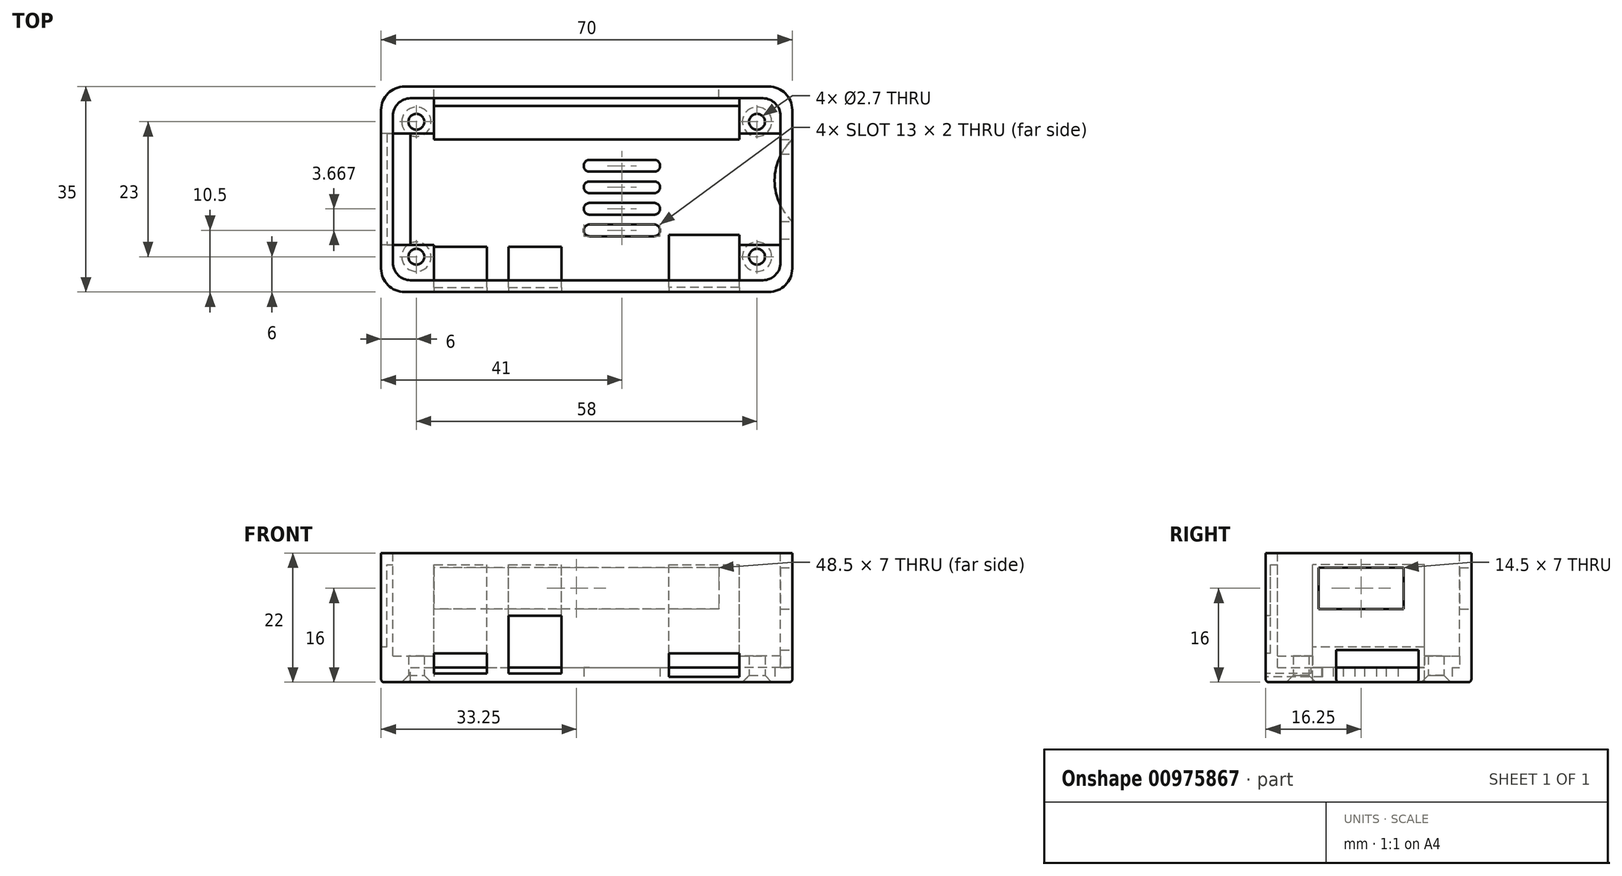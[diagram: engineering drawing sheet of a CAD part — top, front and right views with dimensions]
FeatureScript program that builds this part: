
annotation { "Feature Type Name" : "Feature", "Feature Type Description" : "" }
export const myFeature = defineFeature(function(context is Context, id is Id, definition is map)
    precondition{}
    {
        {
            var Q0;
            Q0=qCreatedBy(makeId("Top.planeOp"),FACE);
            var sketch = newSketch(context, id + "F0", { "sketchPlane" : qUnion([Q0])});
            skLineSegment(sketch, "E0.bottom", {"start": v(-31, 17.5) * mm, "end": v(31, 17.5) * mm});
            skLineSegment(sketch, "E0.top", {"start": v(-31, -17.5) * mm, "end": v(31, -17.5) * mm});
            skLineSegment(sketch, "E0.left", {"start": v(-35, 13.5) * mm, "end": v(-35, -13.5) * mm});
            skLineSegment(sketch, "E0.right", {"start": v(35, 13.5) * mm, "end": v(35, -13.5) * mm});
            skPoint(sketch, "E1.visualSharp", {"position": v(-35, 17.5) * mm});
            skArc(sketch, "E1.filletArc", {"start": v(-31, 17.5) * mm, "mid": v(-33.83, 16.33) * mm, "end": v(-35, 13.5) * mm});
            skPoint(sketch, "E2.visualSharp", {"position": v(35, 17.5) * mm});
            skArc(sketch, "E2.filletArc", {"start": v(35, 13.5) * mm, "mid": v(33.83, 16.33) * mm, "end": v(31, 17.5) * mm});
            skPoint(sketch, "E3.visualSharp", {"position": v(-35, -17.5) * mm});
            skArc(sketch, "E3.filletArc", {"start": v(-35, -13.5) * mm, "mid": v(-33.83, -16.33) * mm, "end": v(-31, -17.5) * mm});
            skPoint(sketch, "E4.visualSharp", {"position": v(35, -17.5) * mm});
            skArc(sketch, "E4.filletArc", {"start": v(31, -17.5) * mm, "mid": v(33.83, -16.33) * mm, "end": v(35, -13.5) * mm});
            skSolve(sketch);
        }
        {
            var Q0;
            Q0=makeQuery(id+"F0.imprint","IMPRINT",FACE,{"disambiguationData":[TD([[makeQuery(id+"F0.imprint","IMPRINT",EDGE,{"derivedFrom":sQuery(id+"F0.wireOp",EDGE,"E0.bottom")}),-1.0]])]});
            extrude(context, id + "F1", {"entities" : qUnion([Q0]), "depth" : 22 * mm, "offsetDistance" : 25 * mm});
        }
        {
            var Q0;
            Q0=makeQuery(id+"F1.opExtrude","CAP_FACE",FACE,{"disambiguationData":[OSD([sQuery(id+"F0.wireOp",EDGE,"E0.bottom"),sQuery(id+"F0.wireOp",EDGE,"E0.top"),sQuery(id+"F0.wireOp",EDGE,"E0.left"),sQuery(id+"F0.wireOp",EDGE,"E0.right"),sQuery(id+"F0.wireOp",EDGE,"E1.filletArc"),sQuery(id+"F0.wireOp",EDGE,"E2.filletArc"),sQuery(id+"F0.wireOp",EDGE,"E3.filletArc"),sQuery(id+"F0.wireOp",EDGE,"E4.filletArc")])],"isStart":false});
            var sketch = newSketch(context, id + "F2", { "sketchPlane" : qUnion([Q0])});
            skLineSegment(sketch, "E5.bottom", {"start": v(-30, 15.5) * mm, "end": v(30, 15.5) * mm});
            skLineSegment(sketch, "E5.top", {"start": v(-30, -15.5) * mm, "end": v(30, -15.5) * mm});
            skLineSegment(sketch, "E5.left", {"start": v(-33, 12.5) * mm, "end": v(-33, -12.5) * mm});
            skLineSegment(sketch, "E5.right", {"start": v(33, 12.5) * mm, "end": v(33, -12.5) * mm});
            skPoint(sketch, "E6.visualSharp", {"position": v(-33, 15.5) * mm});
            skArc(sketch, "E6.filletArc", {"start": v(-30, 15.5) * mm, "mid": v(-32.12, 14.62) * mm, "end": v(-33, 12.5) * mm});
            skPoint(sketch, "E7.visualSharp", {"position": v(-33, -15.5) * mm});
            skArc(sketch, "E7.filletArc", {"start": v(-33, -12.5) * mm, "mid": v(-32.12, -14.62) * mm, "end": v(-30, -15.5) * mm});
            skPoint(sketch, "E8.visualSharp", {"position": v(33, 15.5) * mm});
            skArc(sketch, "E8.filletArc", {"start": v(33, 12.5) * mm, "mid": v(32.12, 14.62) * mm, "end": v(30, 15.5) * mm});
            skPoint(sketch, "E9.visualSharp", {"position": v(33, -15.5) * mm});
            skArc(sketch, "E9.filletArc", {"start": v(30, -15.5) * mm, "mid": v(32.12, -14.62) * mm, "end": v(33, -12.5) * mm});
            skSolve(sketch);
        }
        {
            var Q0;
            Q0=makeQuery(id+"F2.imprint","IMPRINT",FACE,{"disambiguationData":[TD([[makeQuery(id+"F2.imprint","IMPRINT",EDGE,{"derivedFrom":sQuery(id+"F2.wireOp",EDGE,"E5.bottom")}),-1.0]])]});
            extrude(context, id + "F3", {"entities" : qUnion([Q0]), "operationType" : NewBodyOperationType.REMOVE, "oppositeDirection" : true, "depth" : 19.5 * mm, "offsetDistance" : 25 * mm});
        }
        {
            var Q0;
            Q0=makeQuery(id+"F1.opExtrude","SWEPT_FACE",FACE,{"disambiguationData":[OSD([sQuery(id+"F0.wireOp",EDGE,"E0.top")])]});
            var sketch = newSketch(context, id + "F4", { "sketchPlane" : qUnion([Q0])});
            skLineSegment(sketch, "E10.bottom", {"start": v(-26, 1.5) * mm, "end": v(-17, 1.5) * mm});
            skLineSegment(sketch, "E10.top", {"start": v(-26, 4.9) * mm, "end": v(-17, 4.9) * mm});
            skLineSegment(sketch, "E10.left", {"start": v(-26, 1.5) * mm, "end": v(-26, 4.9) * mm});
            skLineSegment(sketch, "E10.right", {"start": v(-17, 1.5) * mm, "end": v(-17, 4.9) * mm});
            skLineSegment(sketch, "E11.bottom", {"start": v(-13.3, 1.5) * mm, "end": v(-4.3, 1.5) * mm});
            skLineSegment(sketch, "E11.top", {"start": v(-13.3, 11.3) * mm, "end": v(-4.3, 11.3) * mm});
            skLineSegment(sketch, "E11.left", {"start": v(-13.3, 1.5) * mm, "end": v(-13.3, 11.3) * mm});
            skLineSegment(sketch, "E11.right", {"start": v(-4.3, 1.5) * mm, "end": v(-4.3, 11.3) * mm});
            skLineSegment(sketch, "E12.bottom", {"start": v(26, 0.9) * mm, "end": v(14, 0.9) * mm});
            skLineSegment(sketch, "E12.top", {"start": v(26, 4.9) * mm, "end": v(14, 4.9) * mm});
            skLineSegment(sketch, "E12.left", {"start": v(26, 0.9) * mm, "end": v(26, 4.9) * mm});
            skLineSegment(sketch, "E12.right", {"start": v(14, 0.9) * mm, "end": v(14, 4.9) * mm});
            skSolve(sketch);
        }
        {
            var Q0;
            Q0=makeQuery(id+"F4.imprint","IMPRINT",FACE,{"disambiguationData":[TD([[makeQuery(id+"F4.imprint","IMPRINT",EDGE,{"derivedFrom":sQuery(id+"F4.wireOp",EDGE,"E10.bottom")}),1.0]])]});
            extrude(context, id + "F5", {"entities" : qUnion([Q0]), "operationType" : NewBodyOperationType.REMOVE, "oppositeDirection" : true, "depth" : 7.7 * mm, "offsetDistance" : 25 * mm});
        }
        {
            var Q0;
            Q0=makeQuery(id+"F4.imprint","IMPRINT",FACE,{"disambiguationData":[TD([[makeQuery(id+"F4.imprint","IMPRINT",EDGE,{"derivedFrom":sQuery(id+"F4.wireOp",EDGE,"E11.bottom")}),1.0]])]});
            extrude(context, id + "F6", {"entities" : qUnion([Q0]), "operationType" : NewBodyOperationType.REMOVE, "oppositeDirection" : true, "depth" : 7.7 * mm, "offsetDistance" : 25 * mm});
        }
        {
            var Q0;
            Q0=makeQuery(id+"F4.imprint","IMPRINT",FACE,{"disambiguationData":[TD([[makeQuery(id+"F4.imprint","IMPRINT",EDGE,{"derivedFrom":sQuery(id+"F4.wireOp",EDGE,"E12.bottom")}),-1.0]])]});
            extrude(context, id + "F7", {"entities" : qUnion([Q0]), "operationType" : NewBodyOperationType.REMOVE, "oppositeDirection" : true, "depth" : 9.7 * mm, "offsetDistance" : 25 * mm});
        }
        {
            var Q0;
            Q0=makeQuery(id+"F3.boolean.opBoolean","COPY",FACE,{"derivedFrom":makeQuery(id+"F3.opExtrude","CAP_FACE",FACE,{"disambiguationData":[OSD([sQuery(id+"F2.wireOp",EDGE,"E5.bottom"),sQuery(id+"F2.wireOp",EDGE,"E5.top"),sQuery(id+"F2.wireOp",EDGE,"E5.left"),sQuery(id+"F2.wireOp",EDGE,"E5.right"),sQuery(id+"F2.wireOp",EDGE,"E6.filletArc"),sQuery(id+"F2.wireOp",EDGE,"E7.filletArc"),sQuery(id+"F2.wireOp",EDGE,"E8.filletArc"),sQuery(id+"F2.wireOp",EDGE,"E9.filletArc")])],"isStart":false})});
            var sketch = newSketch(context, id + "F8", { "sketchPlane" : qUnion([Q0])});
            skLineSegment(sketch, "E13.bottom", {"start": v(-33, 9.5) * mm, "end": v(-26, 9.5) * mm});
            skLineSegment(sketch, "E13.top", {"start": v(-33, 15.5) * mm, "end": v(-26, 15.5) * mm});
            skLineSegment(sketch, "E13.left", {"start": v(-33, 9.5) * mm, "end": v(-33, 15.5) * mm});
            skLineSegment(sketch, "E13.right", {"start": v(-26, 9.5) * mm, "end": v(-26, 15.5) * mm});
            skLineSegment(sketch, "E14.bottom", {"start": v(-33, -9.5) * mm, "end": v(-26, -9.5) * mm});
            skLineSegment(sketch, "E14.top", {"start": v(-33, -15.5) * mm, "end": v(-26, -15.5) * mm});
            skLineSegment(sketch, "E14.left", {"start": v(-33, -9.5) * mm, "end": v(-33, -15.5) * mm});
            skLineSegment(sketch, "E14.right", {"start": v(-26, -9.5) * mm, "end": v(-26, -15.5) * mm});
            skLineSegment(sketch, "E15.bottom", {"start": v(33, -9.5) * mm, "end": v(26, -9.5) * mm});
            skLineSegment(sketch, "E15.top", {"start": v(33, -15.5) * mm, "end": v(26, -15.5) * mm});
            skLineSegment(sketch, "E15.left", {"start": v(33, -9.5) * mm, "end": v(33, -15.5) * mm});
            skLineSegment(sketch, "E15.right", {"start": v(26, -9.5) * mm, "end": v(26, -15.5) * mm});
            skLineSegment(sketch, "E16.bottom", {"start": v(33, 9.5) * mm, "end": v(26, 9.5) * mm});
            skLineSegment(sketch, "E16.top", {"start": v(33, 15.5) * mm, "end": v(26, 15.5) * mm});
            skLineSegment(sketch, "E16.left", {"start": v(33, 9.5) * mm, "end": v(33, 15.5) * mm});
            skLineSegment(sketch, "E16.right", {"start": v(26, 9.5) * mm, "end": v(26, 15.5) * mm});
            skSolve(sketch);
        }
        {
            var Q0;
            {var subQ2=sQuery(id+"F8.wireOp",EDGE,"E13.bottom");Q0=makeQuery(id+"F8.imprint","IMPRINT",FACE,{"disambiguationData":[TD([[makeQuery(id+"F8.imprint","IMPRINT",EDGE,{"derivedFrom":subQ2}),1.0]])]});}
            var Q1;
            {var subQ3=sQuery(id+"F8.wireOp",EDGE,"E14.bottom");Q1=makeQuery(id+"F8.imprint","IMPRINT",FACE,{"disambiguationData":[TD([[makeQuery(id+"F8.imprint","IMPRINT",EDGE,{"derivedFrom":subQ3}),-1.0]])]});}
            var Q2;
            {var subQ2=sQuery(id+"F8.wireOp",EDGE,"E16.bottom");Q2=makeQuery(id+"F8.imprint","IMPRINT",FACE,{"disambiguationData":[TD([[makeQuery(id+"F8.imprint","IMPRINT",EDGE,{"derivedFrom":subQ2}),-1.0]])]});}
            var Q3;
            {var subQ2=sQuery(id+"F8.wireOp",EDGE,"E15.bottom");Q3=makeQuery(id+"F8.imprint","IMPRINT",FACE,{"disambiguationData":[TD([[makeQuery(id+"F8.imprint","IMPRINT",EDGE,{"derivedFrom":subQ2}),1.0]])]});}
            extrude(context, id + "F9", {"entities" : qUnion([Q0, Q1, Q2, Q3]), "operationType" : NewBodyOperationType.ADD, "depth" : 2 * mm, "offsetDistance" : 25 * mm});
        }
        {
            var Q0;
            Q0=makeQuery(id+"F1.opExtrude","SWEPT_FACE",FACE,{"disambiguationData":[OSD([sQuery(id+"F0.wireOp",EDGE,"E0.right")])]});
            var sketch = newSketch(context, id + "F10", { "sketchPlane" : qUnion([Q0])});
            skLineSegment(sketch, "E17.bottom", {"start": v(8.5, 2.5) * mm, "end": v(-5.5, 2.5) * mm});
            skLineSegment(sketch, "E17.top", {"start": v(8.5, 5.5) * mm, "end": v(-5.5, 5.5) * mm});
            skLineSegment(sketch, "E17.left", {"start": v(8.5, 2.5) * mm, "end": v(8.5, 5.5) * mm});
            skLineSegment(sketch, "E17.right", {"start": v(-5.5, 2.5) * mm, "end": v(-5.5, 5.5) * mm});
            skSolve(sketch);
        }
        {
            var Q0;
            Q0=makeQuery(id+"F10.imprint","IMPRINT",FACE,{"disambiguationData":[TD([[makeQuery(id+"F10.imprint","IMPRINT",EDGE,{"derivedFrom":sQuery(id+"F10.wireOp",EDGE,"E17.bottom")}),-1.0]])]});
            var Q1;
            Q1=makeQuery(id+"F3.boolean.opBoolean","COPY",FACE,{"derivedFrom":makeQuery(id+"F3.opExtrude","SWEPT_FACE",FACE,{"disambiguationData":[OSD([sQuery(id+"F2.wireOp",EDGE,"E5.right")])]})});
            extrude(context, id + "F11", {"entities" : qUnion([Q0]), "operationType" : NewBodyOperationType.REMOVE, "endBound" : BoundingType.UP_TO_SURFACE, "oppositeDirection" : true, "depth" : 25 * mm, "endBoundEntityFace" : qUnion([Q1]), "offsetDistance" : 25 * mm});
        }
        {
            var Q0;
            Q0=makeQuery(id+"F1.opExtrude","CAP_FACE",FACE,{"disambiguationData":[OSD([sQuery(id+"F0.wireOp",EDGE,"E0.bottom"),sQuery(id+"F0.wireOp",EDGE,"E0.top"),sQuery(id+"F0.wireOp",EDGE,"E0.left"),sQuery(id+"F0.wireOp",EDGE,"E0.right"),sQuery(id+"F0.wireOp",EDGE,"E1.filletArc"),sQuery(id+"F0.wireOp",EDGE,"E2.filletArc"),sQuery(id+"F0.wireOp",EDGE,"E3.filletArc"),sQuery(id+"F0.wireOp",EDGE,"E4.filletArc")])],"isStart":true});
            var sketch = newSketch(context, id + "F12", { "sketchPlane" : qUnion([Q0])});
            skPoint(sketch, "E18", {"position": v(35, 5.5) * mm});
            skPoint(sketch, "E19", {"position": v(35, -8.5) * mm});
            skPoint(sketch, "E20", {"position": v(32, -1.5) * mm});
            skArc(sketch, "E21", {"start": v(35, 5.5) * mm, "mid": v(32, -1.5) * mm, "end": v(35, -8.5) * mm});
            skLineSegment(sketch, "E22", {"start": v(35, 5.5) * mm, "end": v(35, -8.5) * mm});
            skSolve(sketch);
        }
        {
            var Q0;
            Q0=makeQuery(id+"F12.imprint","IMPRINT",FACE,{"disambiguationData":[TD([[makeQuery(id+"F12.imprint","IMPRINT",EDGE,{"derivedFrom":sQuery(id+"F12.wireOp",EDGE,"E21")}),1.0]])]});
            extrude(context, id + "F13", {"entities" : qUnion([Q0]), "operationType" : NewBodyOperationType.REMOVE, "oppositeDirection" : true, "depth" : 3 * mm, "offsetDistance" : 25 * mm});
        }
        {
            var Q0;
            Q0=makeQuery(id+"F1.opExtrude","SWEPT_FACE",FACE,{"disambiguationData":[OSD([sQuery(id+"F0.wireOp",EDGE,"E0.left")])]});
            var sketch = newSketch(context, id + "F14", { "sketchPlane" : qUnion([Q0])});
            skLineSegment(sketch, "E23.bottom", {"start": v(-9.5, 0) * mm, "end": v(9.5, 0) * mm});
            skLineSegment(sketch, "E23.top", {"start": v(-9.5, 6) * mm, "end": v(9.5, 6) * mm});
            skLineSegment(sketch, "E23.left", {"start": v(-9.5, 0) * mm, "end": v(-9.5, 6) * mm});
            skLineSegment(sketch, "E23.right", {"start": v(9.5, 0) * mm, "end": v(9.5, 6) * mm});
            skSolve(sketch);
        }
        {
            var Q0;
            Q0=makeQuery(id+"F14.imprint","IMPRINT",FACE,{"disambiguationData":[TD([[makeQuery(id+"F14.imprint","IMPRINT",EDGE,{"derivedFrom":sQuery(id+"F14.wireOp",EDGE,"E23.bottom")}),1.0]])]});
            var Q1;
            Q1=makeQuery(id+"F3.boolean.opBoolean","COPY",FACE,{"derivedFrom":makeQuery(id+"F3.opExtrude","SWEPT_FACE",FACE,{"disambiguationData":[OSD([sQuery(id+"F2.wireOp",EDGE,"E5.left")])]})});
            extrude(context, id + "F15", {"entities" : qUnion([Q0]), "operationType" : NewBodyOperationType.REMOVE, "oppositeDirection" : true, "depth" : 5 * mm, "endBoundEntityFace" : qUnion([Q1]), "offsetDistance" : 25 * mm});
        }
        {
            var Q0;
            Q0=makeQuery(id+"F1.opExtrude","SWEPT_FACE",FACE,{"disambiguationData":[OSD([sQuery(id+"F0.wireOp",EDGE,"E0.bottom")])]});
            var sketch = newSketch(context, id + "F16", { "sketchPlane" : qUnion([Q0])});
            skLineSegment(sketch, "E24.bottom", {"start": v(-22.5, 19.5) * mm, "end": v(26, 19.5) * mm});
            skLineSegment(sketch, "E24.top", {"start": v(-22.5, 12.5) * mm, "end": v(26, 12.5) * mm});
            skLineSegment(sketch, "E24.left", {"start": v(-22.5, 19.5) * mm, "end": v(-22.5, 12.5) * mm});
            skLineSegment(sketch, "E24.right", {"start": v(26, 19.5) * mm, "end": v(26, 12.5) * mm});
            skSolve(sketch);
        }
        {
            var Q0;
            Q0=makeQuery(id+"F16.imprint","IMPRINT",FACE,{"disambiguationData":[TD([[makeQuery(id+"F16.imprint","IMPRINT",EDGE,{"derivedFrom":sQuery(id+"F16.wireOp",EDGE,"E24.bottom")}),-1.0]])]});
            extrude(context, id + "F17", {"entities" : qUnion([Q0]), "operationType" : NewBodyOperationType.REMOVE, "endBound" : BoundingType.UP_TO_NEXT, "oppositeDirection" : true, "depth" : 25 * mm, "offsetDistance" : 25 * mm});
        }
        {
            var Q0;
            Q0=makeQuery(id+"F1.opExtrude","SWEPT_FACE",FACE,{"disambiguationData":[OSD([sQuery(id+"F0.wireOp",EDGE,"E0.right")])]});
            var sketch = newSketch(context, id + "F18", { "sketchPlane" : qUnion([Q0])});
            skLineSegment(sketch, "E25.bottom", {"start": v(-8.5, 19.5) * mm, "end": v(6, 19.5) * mm});
            skLineSegment(sketch, "E25.top", {"start": v(-8.5, 12.5) * mm, "end": v(6, 12.5) * mm});
            skLineSegment(sketch, "E25.left", {"start": v(-8.5, 19.5) * mm, "end": v(-8.5, 12.5) * mm});
            skLineSegment(sketch, "E25.right", {"start": v(6, 19.5) * mm, "end": v(6, 12.5) * mm});
            skSolve(sketch);
        }
        {
            var Q0;
            Q0=makeQuery(id+"F18.imprint","IMPRINT",FACE,{"disambiguationData":[TD([[makeQuery(id+"F18.imprint","IMPRINT",EDGE,{"derivedFrom":sQuery(id+"F18.wireOp",EDGE,"E25.bottom")}),-1.0]])]});
            extrude(context, id + "F19", {"entities" : qUnion([Q0]), "operationType" : NewBodyOperationType.REMOVE, "endBound" : BoundingType.UP_TO_NEXT, "oppositeDirection" : true, "depth" : 25 * mm, "offsetDistance" : 25 * mm});
        }
        {
            var Q0;
            Q0=makeQuery(id+"F1.opExtrude","CAP_FACE",FACE,{"disambiguationData":[OSD([sQuery(id+"F0.wireOp",EDGE,"E0.bottom"),sQuery(id+"F0.wireOp",EDGE,"E0.top"),sQuery(id+"F0.wireOp",EDGE,"E0.left"),sQuery(id+"F0.wireOp",EDGE,"E0.right"),sQuery(id+"F0.wireOp",EDGE,"E1.filletArc"),sQuery(id+"F0.wireOp",EDGE,"E2.filletArc"),sQuery(id+"F0.wireOp",EDGE,"E3.filletArc"),sQuery(id+"F0.wireOp",EDGE,"E4.filletArc")])],"isStart":true});
            var sketch = newSketch(context, id + "F20", { "sketchPlane" : qUnion([Q0])});
            skPoint(sketch, "E26", {"position": v(-29, 11.5) * mm});
            skPoint(sketch, "E27", {"position": v(-29, -11.5) * mm});
            skPoint(sketch, "E28", {"position": v(29, -11.5) * mm});
            skPoint(sketch, "E29", {"position": v(29, 11.5) * mm});
            skSolve(sketch);
        }
        {
            var Q0;
            Q0=sQuery(id+"F20.wireOp",VERTEX,"E26");
            var Q1;
            Q1=makeQuery(id+"F1.opExtrude","SWEPT_BODY",BODY,{"disambiguationData":[OSD([sQuery(id+"F0.wireOp",EDGE,"E0.bottom"),sQuery(id+"F0.wireOp",EDGE,"E0.top"),sQuery(id+"F0.wireOp",EDGE,"E0.left"),sQuery(id+"F0.wireOp",EDGE,"E0.right"),sQuery(id+"F0.wireOp",EDGE,"E1.filletArc"),sQuery(id+"F0.wireOp",EDGE,"E2.filletArc"),sQuery(id+"F0.wireOp",EDGE,"E3.filletArc"),sQuery(id+"F0.wireOp",EDGE,"E4.filletArc")])]});
            hole(context, id + "F21", {"style" : HoleStyle.C_SINK, "endStyle" : HoleEndStyle.THROUGH, "holeDiameter" : 2.7 * mm, "cSinkDiameter" : 5 * mm, "cSinkAngle" : 90 * degree, "majorDiameter" : 5 * mm, "isTappedThrough" : true, "tappedDepth" : 12 * mm, "tapClearance" : 3, "startFromSketch" : true, "locations" : qUnion([Q0]), "scope" : qUnion([Q1])});
        }
        {
            var Q0;
            Q0=sQuery(id+"F20.wireOp",VERTEX,"E29");
            var Q1;
            Q1=sQuery(id+"F20.wireOp",VERTEX,"E28");
            var Q2;
            Q2=sQuery(id+"F20.wireOp",VERTEX,"E27");
            var Q3;
            Q3=makeQuery(id+"F1.opExtrude","SWEPT_BODY",BODY,{"disambiguationData":[OSD([sQuery(id+"F0.wireOp",EDGE,"E0.bottom"),sQuery(id+"F0.wireOp",EDGE,"E0.top"),sQuery(id+"F0.wireOp",EDGE,"E0.left"),sQuery(id+"F0.wireOp",EDGE,"E0.right"),sQuery(id+"F0.wireOp",EDGE,"E1.filletArc"),sQuery(id+"F0.wireOp",EDGE,"E2.filletArc"),sQuery(id+"F0.wireOp",EDGE,"E3.filletArc"),sQuery(id+"F0.wireOp",EDGE,"E4.filletArc")])]});
            hole(context, id + "F22", {"style" : HoleStyle.C_SINK, "endStyle" : HoleEndStyle.THROUGH, "holeDiameter" : 2.7 * mm, "cSinkDiameter" : 5 * mm, "cSinkAngle" : 90 * degree, "majorDiameter" : 5 * mm, "isTappedThrough" : true, "tappedDepth" : 12 * mm, "tapClearance" : 3, "startFromSketch" : true, "locations" : qUnion([Q0, Q1, Q2]), "scope" : qUnion([Q3])});
        }
        {
            var Q0;
            {var subQ3=sQuery(id+"F0.wireOp",EDGE,"E0.bottom");Q0=makeQuery(id+"F20.imprint","IMPRINT",FACE,{"disambiguationData":[TD([[makeQuery(id+"F20.imprint","IMPRINT",EDGE,{"derivedFrom":makeQuery(id+"F1.opExtrude","CAP_EDGE",EDGE,{"disambiguationData":[OSD([subQ3])],"isStart":true})}),1.0]])]});}
            var sketch = newSketch(context, id + "F23", { "sketchPlane" : qUnion([Q0])});
            skLineSegment(sketch, "E30.bottom", {"start": v(-26, -8.5) * mm, "end": v(26, -8.5) * mm});
            skLineSegment(sketch, "E30.top", {"start": v(-26, -14.2) * mm, "end": v(26, -14.2) * mm});
            skLineSegment(sketch, "E30.left", {"start": v(-26, -8.5) * mm, "end": v(-26, -14.2) * mm});
            skLineSegment(sketch, "E30.right", {"start": v(26, -8.5) * mm, "end": v(26, -14.2) * mm});
            skSolve(sketch);
        }
        {
            var Q0;
            Q0=makeQuery(id+"F23.imprint","IMPRINT",FACE,{"disambiguationData":[TD([[makeQuery(id+"F23.imprint","IMPRINT",EDGE,{"derivedFrom":sQuery(id+"F23.wireOp",EDGE,"E30.bottom")}),-1.0]])]});
            extrude(context, id + "F24", {"entities" : qUnion([Q0]), "operationType" : NewBodyOperationType.REMOVE, "endBound" : BoundingType.UP_TO_NEXT, "oppositeDirection" : true, "depth" : 25 * mm, "offsetDistance" : 25 * mm});
        }
        {
            var Q0;
            {var subQ3=sQuery(id+"F0.wireOp",EDGE,"E0.bottom");Q0=makeQuery(id+"F20.imprint","IMPRINT",FACE,{"disambiguationData":[TD([[makeQuery(id+"F20.imprint","IMPRINT",EDGE,{"derivedFrom":makeQuery(id+"F1.opExtrude","CAP_EDGE",EDGE,{"disambiguationData":[OSD([subQ3])],"isStart":true})}),1.0]])]});}
            var sketch = newSketch(context, id + "F25", { "sketchPlane" : qUnion([Q0])});
            skLineSegment(sketch, "E31", {"start": v(0.5, 8) * mm, "end": v(11.5, 8) * mm});
            skArc(sketch, "E32", {"start": v(11.5, 8) * mm, "mid": v(12.5, 7) * mm, "end": v(11.5, 6) * mm});
            skArc(sketch, "E33", {"start": v(0.5, 8) * mm, "mid": v(-0.5, 7) * mm, "end": v(0.5, 6) * mm});
            skLineSegment(sketch, "E34", {"start": v(0.5, 6) * mm, "end": v(11.5, 6) * mm});
            skLineSegment(sketch, "E35.1.0.0", {"start": v(0.5, 2.33) * mm, "end": v(11.5, 2.33) * mm});
            skArc(sketch, "E35.1.0.1", {"start": v(0.5, 4.33) * mm, "mid": v(-0.5, 3.33) * mm, "end": v(0.5, 2.33) * mm});
            skArc(sketch, "E35.1.0.2", {"start": v(11.5, 4.33) * mm, "mid": v(12.5, 3.33) * mm, "end": v(11.5, 2.33) * mm});
            skLineSegment(sketch, "E35.1.0.3", {"start": v(0.5, 4.33) * mm, "end": v(11.5, 4.33) * mm});
            skLineSegment(sketch, "E35.2.0.0", {"start": v(0.5, -1.33) * mm, "end": v(11.5, -1.33) * mm});
            skArc(sketch, "E35.2.0.1", {"start": v(0.5, 0.67) * mm, "mid": v(-0.5, -0.33) * mm, "end": v(0.5, -1.33) * mm});
            skArc(sketch, "E35.2.0.2", {"start": v(11.5, 0.67) * mm, "mid": v(12.5, -0.33) * mm, "end": v(11.5, -1.33) * mm});
            skLineSegment(sketch, "E35.2.0.3", {"start": v(0.5, 0.67) * mm, "end": v(11.5, 0.67) * mm});
            skLineSegment(sketch, "E35.3.0.0", {"start": v(0.5, -5) * mm, "end": v(11.5, -5) * mm});
            skArc(sketch, "E35.3.0.1", {"start": v(0.5, -3) * mm, "mid": v(-0.5, -4) * mm, "end": v(0.5, -5) * mm});
            skArc(sketch, "E35.3.0.2", {"start": v(11.5, -3) * mm, "mid": v(12.5, -4) * mm, "end": v(11.5, -5) * mm});
            skLineSegment(sketch, "E35.3.0.3", {"start": v(0.5, -3) * mm, "end": v(11.5, -3) * mm});
            skLineSegment(sketch, "E35.direction1", {"start": v(0.5, 6) * mm, "end": v(0.5, 2.33) * mm, "construction": true});
            skSolve(sketch);
        }
        {
            var Q0;
            Q0=makeQuery(id+"F25.imprint","IMPRINT",FACE,{"disambiguationData":[TD([[makeQuery(id+"F25.imprint","IMPRINT",EDGE,{"derivedFrom":sQuery(id+"F25.wireOp",EDGE,"E35.2.0.0")}),1.0]])]});
            var Q1;
            Q1=makeQuery(id+"F25.imprint","IMPRINT",FACE,{"disambiguationData":[TD([[makeQuery(id+"F25.imprint","IMPRINT",EDGE,{"derivedFrom":sQuery(id+"F25.wireOp",EDGE,"E35.1.0.0")}),1.0]])]});
            var Q2;
            Q2=makeQuery(id+"F25.imprint","IMPRINT",FACE,{"disambiguationData":[TD([[makeQuery(id+"F25.imprint","IMPRINT",EDGE,{"derivedFrom":sQuery(id+"F25.wireOp",EDGE,"E35.3.0.0")}),1.0]])]});
            var Q3;
            Q3=makeQuery(id+"F25.imprint","IMPRINT",FACE,{"disambiguationData":[TD([[makeQuery(id+"F25.imprint","IMPRINT",EDGE,{"derivedFrom":sQuery(id+"F25.wireOp",EDGE,"E31")}),-1.0]])]});
            extrude(context, id + "F26", {"entities" : qUnion([Q0, Q1, Q2, Q3]), "operationType" : NewBodyOperationType.REMOVE, "endBound" : BoundingType.UP_TO_NEXT, "oppositeDirection" : true, "depth" : 25 * mm, "offsetDistance" : 25 * mm});
        }
        {
            var Q0;
            Q0=makeQuery(id+"F3.boolean.opBoolean","COPY",FACE,{"derivedFrom":makeQuery(id+"F3.opExtrude","SWEPT_FACE",FACE,{"disambiguationData":[OSD([sQuery(id+"F2.wireOp",EDGE,"E5.left")])]})});
            var sketch = newSketch(context, id + "F27", { "sketchPlane" : qUnion([Q0])});
            skLineSegment(sketch, "E36.bottom", {"start": v(9.5, 6) * mm, "end": v(-9.5, 6) * mm});
            skLineSegment(sketch, "E36.top", {"start": v(9.5, 20) * mm, "end": v(-9.5, 20) * mm});
            skLineSegment(sketch, "E36.left", {"start": v(9.5, 6) * mm, "end": v(9.5, 20) * mm});
            skLineSegment(sketch, "E36.right", {"start": v(-9.5, 6) * mm, "end": v(-9.5, 20) * mm});
            skSolve(sketch);
        }
        {
            var Q0;
            Q0 = qSketchRegion(id + "F27", true);
            extrude(context, id + "F28", {"entities" : qUnion([Q0]), "operationType" : NewBodyOperationType.REMOVE, "oppositeDirection" : true, "depth" : 1 * mm, "offsetDistance" : 25 * mm});
        }
        {
            var Q0;
            Q0=makeQuery(id+"F3.boolean.opBoolean","COPY",FACE,{"derivedFrom":makeQuery(id+"F3.opExtrude","SWEPT_FACE",FACE,{"disambiguationData":[OSD([sQuery(id+"F2.wireOp",EDGE,"E5.top")])]})});
            var sketch = newSketch(context, id + "F29", { "sketchPlane" : qUnion([Q0])});
            skLineSegment(sketch, "E37.bottom", {"start": v(26, 4.9) * mm, "end": v(17, 4.9) * mm});
            skLineSegment(sketch, "E37.top", {"start": v(26, 20) * mm, "end": v(17, 20) * mm});
            skLineSegment(sketch, "E37.left", {"start": v(26, 4.9) * mm, "end": v(26, 20) * mm});
            skLineSegment(sketch, "E37.right", {"start": v(17, 4.9) * mm, "end": v(17, 20) * mm});
            skLineSegment(sketch, "E38.bottom", {"start": v(13.3, 11.3) * mm, "end": v(4.3, 11.3) * mm});
            skLineSegment(sketch, "E38.top", {"start": v(13.3, 20) * mm, "end": v(4.3, 20) * mm});
            skLineSegment(sketch, "E38.left", {"start": v(13.3, 11.3) * mm, "end": v(13.3, 20) * mm});
            skLineSegment(sketch, "E38.right", {"start": v(4.3, 11.3) * mm, "end": v(4.3, 20) * mm});
            skLineSegment(sketch, "E39.bottom", {"start": v(-14, 4.9) * mm, "end": v(-26, 4.9) * mm});
            skLineSegment(sketch, "E39.top", {"start": v(-14, 20) * mm, "end": v(-26, 20) * mm});
            skLineSegment(sketch, "E39.left", {"start": v(-14, 4.9) * mm, "end": v(-14, 20) * mm});
            skLineSegment(sketch, "E39.right", {"start": v(-26, 4.9) * mm, "end": v(-26, 20) * mm});
            skSolve(sketch);
        }
        {
            var Q0;
            Q0 = qSketchRegion(id + "F29", true);
            extrude(context, id + "F30", {"entities" : qUnion([Q0]), "operationType" : NewBodyOperationType.REMOVE, "oppositeDirection" : true, "depth" : 1.2 * mm, "offsetDistance" : 25 * mm});
        }
        {
            var Q0;
            Q0=makeQuery(id+"F1.opExtrude","CAP_EDGE",EDGE,{"disambiguationData":[OSD([sQuery(id+"F0.wireOp",EDGE,"E0.top")])],"isStart":true});
            var Q1;
            Q1=makeQuery(id+"F1.opExtrude","CAP_EDGE",EDGE,{"disambiguationData":[OSD([sQuery(id+"F0.wireOp",EDGE,"E4.filletArc")])],"isStart":true});
            var Q2;
            {var subQ0=sQuery(id+"F0.wireOp",EDGE,"E4.filletArc");var subQ1=sQuery(id+"F0.wireOp",EDGE,"E0.right");Q2=makeQuery(id+"F13.boolean.opBoolean","SPLIT",EDGE,{"disambiguationData":[TD([makeQuery(id+"F1.opExtrude","SWEPT_FACE",FACE,{"disambiguationData":[OSD([subQ0])]})])],"derivedFrom":makeQuery(id+"F1.opExtrude","CAP_EDGE",EDGE,{"disambiguationData":[OSD([subQ1])],"isStart":true})});}
            var Q3;
            Q3=makeQuery(id+"F13.boolean.opBoolean","COPY",EDGE,{"derivedFrom":makeQuery(id+"F13.opExtrude","CAP_EDGE",EDGE,{"disambiguationData":[OSD([sQuery(id+"F12.wireOp",EDGE,"E21")])],"isStart":true})});
            var Q4;
            {var subQ0=sQuery(id+"F0.wireOp",EDGE,"E2.filletArc");var subQ1=sQuery(id+"F0.wireOp",EDGE,"E0.right");Q4=makeQuery(id+"F13.boolean.opBoolean","SPLIT",EDGE,{"disambiguationData":[TD([makeQuery(id+"F1.opExtrude","SWEPT_FACE",FACE,{"disambiguationData":[OSD([subQ0])]})])],"derivedFrom":makeQuery(id+"F1.opExtrude","CAP_EDGE",EDGE,{"disambiguationData":[OSD([subQ1])],"isStart":true})});}
            var Q5;
            Q5=makeQuery(id+"F1.opExtrude","CAP_EDGE",EDGE,{"disambiguationData":[OSD([sQuery(id+"F0.wireOp",EDGE,"E2.filletArc")])],"isStart":true});
            var Q6;
            Q6=makeQuery(id+"F1.opExtrude","CAP_EDGE",EDGE,{"disambiguationData":[OSD([sQuery(id+"F0.wireOp",EDGE,"E0.bottom")])],"isStart":true});
            var Q7;
            Q7=makeQuery(id+"F1.opExtrude","CAP_EDGE",EDGE,{"disambiguationData":[OSD([sQuery(id+"F0.wireOp",EDGE,"E1.filletArc")])],"isStart":true});
            var Q8;
            Q8=makeQuery(id+"F15.boolean.opBoolean","COPY",EDGE,{"derivedFrom":makeQuery(id+"F15.opExtrude","SWEPT_EDGE",EDGE,{"disambiguationData":[OSD([sQuery(id+"F0.wireOp",EDGE,"E0.left"),sQuery(id+"F14.wireOp",EDGE,"E23.bottom"),sQuery(id+"F14.wireOp",EDGE,"E23.left")])]})});
            var Q9;
            Q9=makeQuery(id+"F15.boolean.opBoolean","COPY",EDGE,{"derivedFrom":makeQuery(id+"F15.opExtrude","CAP_EDGE",EDGE,{"disambiguationData":[OSD([sQuery(id+"F14.wireOp",EDGE,"E23.bottom")])],"isStart":false})});
            var Q10;
            {var subQ0=sQuery(id+"F0.wireOp",EDGE,"E0.left");var subQ1=sQuery(id+"F0.wireOp",EDGE,"E1.filletArc");Q10=makeQuery(id+"F15.boolean.opBoolean","SPLIT",EDGE,{"disambiguationData":[TD([makeQuery(id+"F1.opExtrude","SWEPT_FACE",FACE,{"disambiguationData":[OSD([subQ1])]})])],"derivedFrom":makeQuery(id+"F1.opExtrude","CAP_EDGE",EDGE,{"disambiguationData":[OSD([subQ0])],"isStart":true})});}
            var Q11;
            Q11=makeQuery(id+"F1.opExtrude","CAP_EDGE",EDGE,{"disambiguationData":[OSD([sQuery(id+"F0.wireOp",EDGE,"E3.filletArc")])],"isStart":true});
            var Q12;
            {var subQ0=sQuery(id+"F0.wireOp",EDGE,"E3.filletArc");var subQ1=sQuery(id+"F0.wireOp",EDGE,"E0.left");Q12=makeQuery(id+"F15.boolean.opBoolean","SPLIT",EDGE,{"disambiguationData":[TD([makeQuery(id+"F1.opExtrude","SWEPT_FACE",FACE,{"disambiguationData":[OSD([subQ0])]})])],"derivedFrom":makeQuery(id+"F1.opExtrude","CAP_EDGE",EDGE,{"disambiguationData":[OSD([subQ1])],"isStart":true})});}
            var Q13;
            Q13=makeQuery(id+"F15.boolean.opBoolean","COPY",EDGE,{"derivedFrom":makeQuery(id+"F15.opExtrude","SWEPT_EDGE",EDGE,{"disambiguationData":[OSD([sQuery(id+"F0.wireOp",EDGE,"E0.left"),sQuery(id+"F14.wireOp",EDGE,"E23.bottom"),sQuery(id+"F14.wireOp",EDGE,"E23.right")])]})});
            fillet(context, id + "F31", {"entities" : qUnion([Q0, Q1, Q2, Q3, Q4, Q5, Q6, Q7, Q8, Q9, Q10, Q11, Q12, Q13]), "radius" : .5 * mm, "tangentPropagation" : true, "allowEdgeOverflow" : false});
        }
    });
